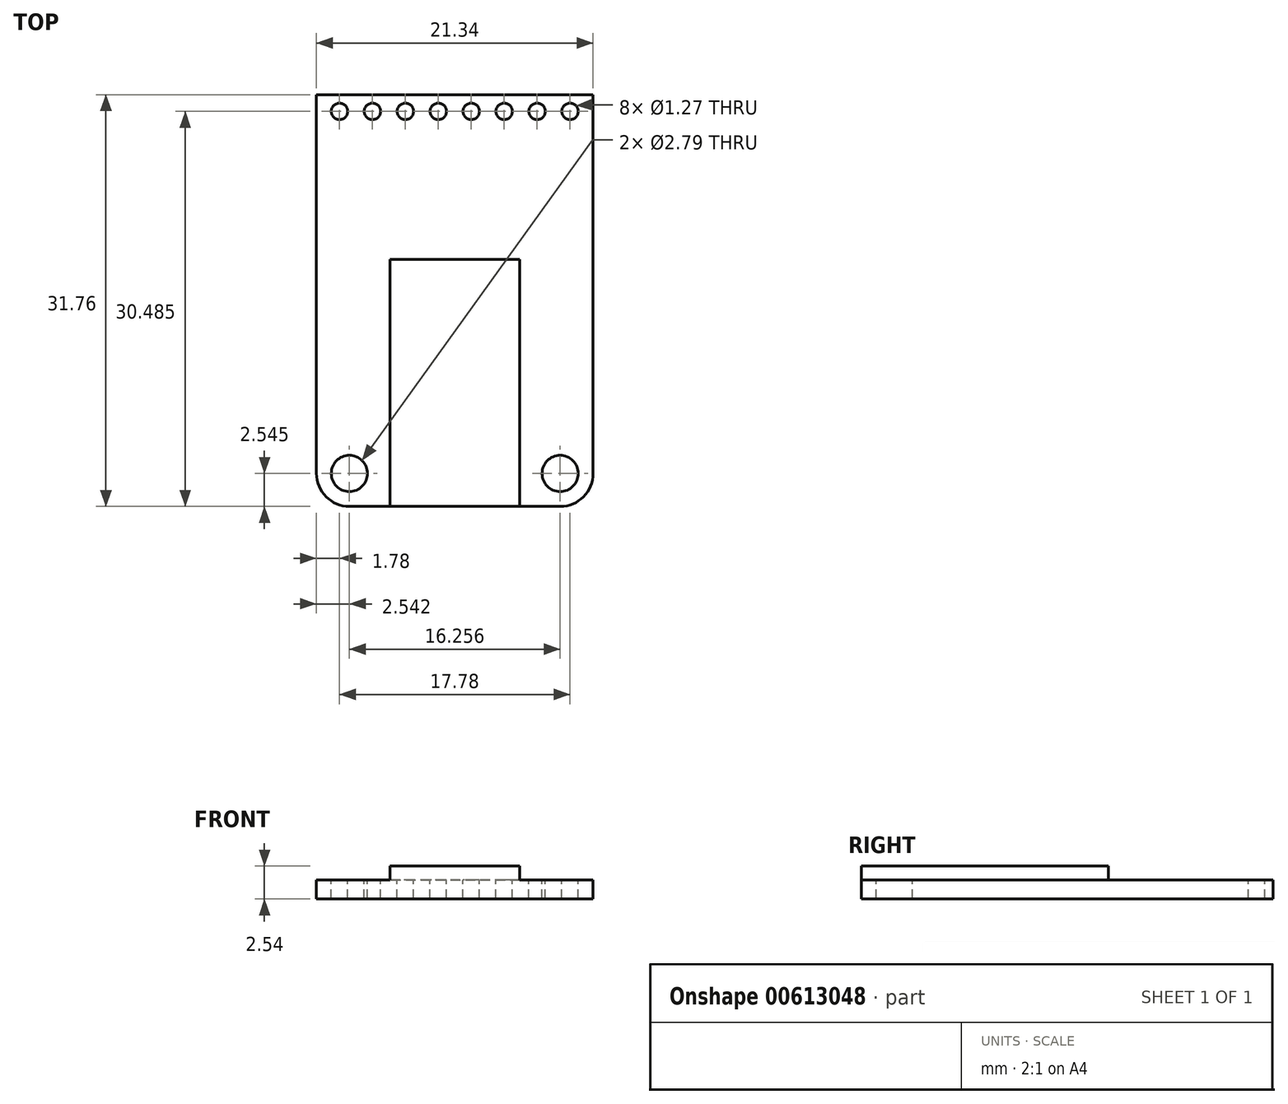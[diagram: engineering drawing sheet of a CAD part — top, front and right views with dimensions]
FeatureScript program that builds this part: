
annotation { "Feature Type Name" : "Feature", "Feature Type Description" : "" }
export const myFeature = defineFeature(function(context is Context, id is Id, definition is map)
    precondition{}
    {
        {
            var Q0;
            Q0=qCreatedBy(makeId("Top.planeOp"),FACE);
            var sketch = newSketch(context, id + "F0", { "sketchPlane" : qUnion([Q0])});
            skLineSegment(sketch, "E0.bottom", {"start": v(-10.67, 15.88) * mm, "end": v(10.67, 15.88) * mm});
            skLineSegment(sketch, "E0.top", {"start": v(-10.67, -15.88) * mm, "end": v(10.67, -15.88) * mm});
            skLineSegment(sketch, "E0.left", {"start": v(-10.67, 15.88) * mm, "end": v(-10.67, -15.88) * mm});
            skLineSegment(sketch, "E0.right", {"start": v(10.67, 15.88) * mm, "end": v(10.67, -15.88) * mm});
            skLineSegment(sketch, "E1", {"start": v(10.67, 15.88) * mm, "end": v(-10.67, -15.88) * mm, "construction": true});
            skSolve(sketch);
        }
        {
            var Q0;
            Q0 = qSketchRegion(id + "F0", true);
            var Q1;
            Q1=makeQuery(id+"F0.imprint","IMPRINT",FACE,{"disambiguationData":[TD([[makeQuery(id+"F0.imprint","IMPRINT",EDGE,{"derivedFrom":sQuery(id+"F0.wireOp",EDGE,"E0.bottom")}),-1.0]])]});
            extrude(context, id + "F1", {"entities" : qUnion([Q0, Q1]), "depth" : 1.47 * mm, "offsetDistance" : 25.4 * mm});
        }
        {
            var Q0;
            Q0=makeQuery(id+"F1.opExtrude","SWEPT_EDGE",EDGE,{"disambiguationData":[OSD([sQuery(id+"F0.wireOp",EDGE,"E0.top"),sQuery(id+"F0.wireOp",EDGE,"E0.right")])]});
            var Q1;
            Q1=makeQuery(id+"F1.opExtrude","SWEPT_EDGE",EDGE,{"disambiguationData":[OSD([sQuery(id+"F0.wireOp",EDGE,"E0.top"),sQuery(id+"F0.wireOp",EDGE,"E0.left")])]});
            fillet(context, id + "F2", {"entities" : qUnion([Q0, Q1]), "radius" : 2.54 * mm, "tangentPropagation" : true, "allowEdgeOverflow" : false});
        }
        {
            var Q0;
            Q0=makeQuery(id+"F1.opExtrude","CAP_FACE",FACE,{"disambiguationData":[OSD([sQuery(id+"F0.wireOp",EDGE,"E0.bottom"),sQuery(id+"F0.wireOp",EDGE,"E0.top"),sQuery(id+"F0.wireOp",EDGE,"E0.left"),sQuery(id+"F0.wireOp",EDGE,"E0.right")])],"isStart":false});
            var sketch = newSketch(context, id + "F3", { "sketchPlane" : qUnion([Q0])});
            skCircle(sketch, "E2", {"center": v(8.13, -13.33) * mm, "radius": 1.4 * mm});
            skLineSegment(sketch, "E3", {"start": v(0, 0) * mm, "end": v(0, -15.48) * mm, "construction": true});
            skCircle(sketch, "E4.MirrorC", {"center": v(-8.13, -13.33) * mm, "radius": 1.4 * mm});
            skSolve(sketch);
        }
        {
            var Q0;
            Q0 = qSketchRegion(id + "F3", true);
            extrude(context, id + "F4", {"entities" : qUnion([Q0]), "operationType" : NewBodyOperationType.REMOVE, "endBound" : BoundingType.UP_TO_NEXT, "oppositeDirection" : true, "depth" : 25.4 * mm, "offsetDistance" : 25.4 * mm});
        }
        {
            var Q0;
            Q0=makeQuery(id+"F1.opExtrude","CAP_FACE",FACE,{"disambiguationData":[OSD([sQuery(id+"F0.wireOp",EDGE,"E0.bottom"),sQuery(id+"F0.wireOp",EDGE,"E0.top"),sQuery(id+"F0.wireOp",EDGE,"E0.left"),sQuery(id+"F0.wireOp",EDGE,"E0.right")])],"isStart":false});
            var sketch = newSketch(context, id + "F5", { "sketchPlane" : qUnion([Q0])});
            skCircle(sketch, "E5", {"center": v(-8.89, 14.6) * mm, "radius": 0.64 * mm});
            skCircle(sketch, "E6.1.0.0", {"center": v(-6.35, 14.6) * mm, "radius": 0.64 * mm});
            skCircle(sketch, "E6.2.0.0", {"center": v(-3.8, 14.6) * mm, "radius": 0.64 * mm});
            skCircle(sketch, "E6.3.0.0", {"center": v(-1.27, 14.6) * mm, "radius": 0.64 * mm});
            skCircle(sketch, "E6.4.0.0", {"center": v(1.27, 14.6) * mm, "radius": 0.64 * mm});
            skCircle(sketch, "E6.5.0.0", {"center": v(3.81, 14.6) * mm, "radius": 0.64 * mm});
            skCircle(sketch, "E6.6.0.0", {"center": v(6.35, 14.6) * mm, "radius": 0.64 * mm});
            skCircle(sketch, "E6.7.0.0", {"center": v(8.9, 14.6) * mm, "radius": 0.64 * mm});
            skLineSegment(sketch, "E6.direction1", {"start": v(-8.89, 14.6) * mm, "end": v(-6.35, 14.6) * mm, "construction": true});
            skLineSegment(sketch, "E7", {"start": v(0, 15.88) * mm, "end": v(0, 0) * mm, "construction": true});
            skSolve(sketch);
        }
        {
            var Q0;
            Q0 = qSketchRegion(id + "F5", true);
            extrude(context, id + "F6", {"entities" : qUnion([Q0]), "operationType" : NewBodyOperationType.REMOVE, "endBound" : BoundingType.UP_TO_NEXT, "oppositeDirection" : true, "depth" : 25.4 * mm, "offsetDistance" : 25.4 * mm});
        }
        {
            var Q0;
            Q0=makeQuery(id+"F1.opExtrude","CAP_FACE",FACE,{"disambiguationData":[OSD([sQuery(id+"F0.wireOp",EDGE,"E0.bottom"),sQuery(id+"F0.wireOp",EDGE,"E0.top"),sQuery(id+"F0.wireOp",EDGE,"E0.left"),sQuery(id+"F0.wireOp",EDGE,"E0.right")])],"isStart":true});
            var sketch = newSketch(context, id + "F7", { "sketchPlane" : qUnion([Q0])});
            skLineSegment(sketch, "E8.bottom", {"start": v(-5, -3.18) * mm, "end": v(5, -3.18) * mm});
            skLineSegment(sketch, "E8.top", {"start": v(-5, 15.88) * mm, "end": v(5, 15.88) * mm});
            skLineSegment(sketch, "E8.left", {"start": v(-5, -3.18) * mm, "end": v(-5, 15.88) * mm});
            skLineSegment(sketch, "E8.right", {"start": v(5, -3.18) * mm, "end": v(5, 15.88) * mm});
            skLineSegment(sketch, "E9", {"start": v(0, 15.88) * mm, "end": v(0, -15.88) * mm, "construction": true});
            skSolve(sketch);
        }
        {
            var Q0;
            Q0 = qSketchRegion(id + "F7", true);
            extrude(context, id + "F8", {"entities" : qUnion([Q0]), "operationType" : NewBodyOperationType.ADD, "oppositeDirection" : true, "depth" : 2.54 * mm, "offsetDistance" : 25.4 * mm});
        }
    });
